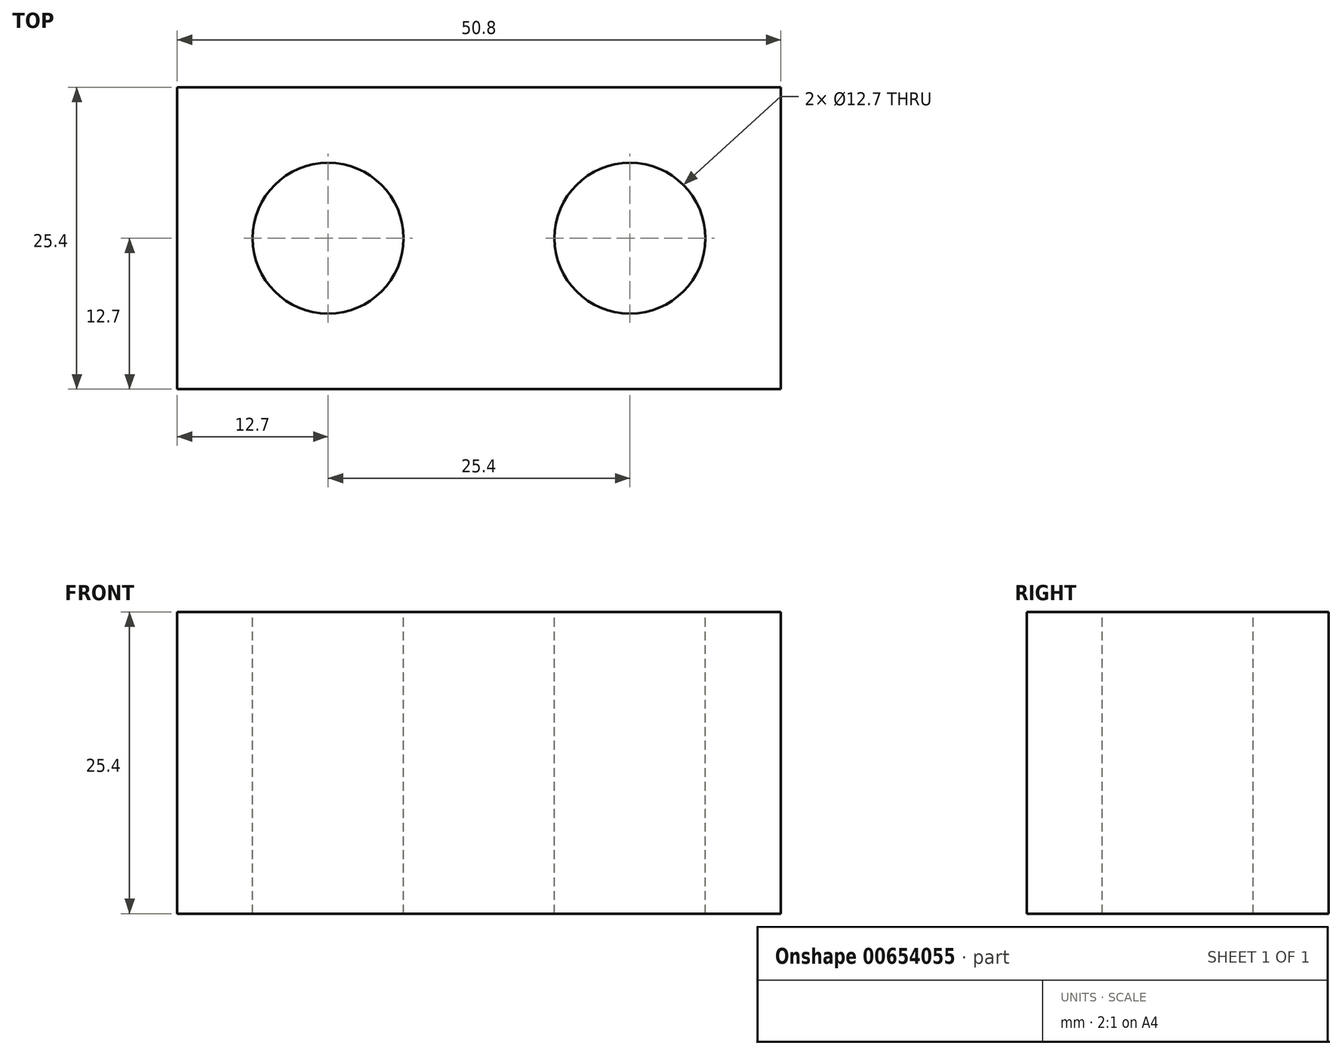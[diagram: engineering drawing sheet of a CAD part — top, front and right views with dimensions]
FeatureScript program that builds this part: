
annotation { "Feature Type Name" : "Feature", "Feature Type Description" : "" }
export const myFeature = defineFeature(function(context is Context, id is Id, definition is map)
    precondition{}
    {
        {
            var Q0;
            Q0=qCreatedBy(makeId("Top.planeOp"),FACE);
            var sketch = newSketch(context, id + "F0", { "sketchPlane" : qUnion([Q0])});
            skLineSegment(sketch, "E0.bottom", {"start": v(0, 0) * mm, "end": v(-50.8, 0) * mm});
            skLineSegment(sketch, "E0.top", {"start": v(0, 25.4) * mm, "end": v(-50.8, 25.4) * mm});
            skLineSegment(sketch, "E0.left", {"start": v(0, 0) * mm, "end": v(0, 25.4) * mm});
            skLineSegment(sketch, "E0.right", {"start": v(-50.8, 0) * mm, "end": v(-50.8, 25.4) * mm});
            skLineSegment(sketch, "E1", {"start": v(-25.4, 25.4) * mm, "end": v(-25.4, 0) * mm, "construction": true});
            skLineSegment(sketch, "E2", {"start": v(-25.4, 0) * mm, "end": v(-50.8, 25.4) * mm, "construction": true});
            skLineSegment(sketch, "E3", {"start": v(0, 25.4) * mm, "end": v(-25.4, 0) * mm, "construction": true});
            skCircle(sketch, "E4", {"center": v(-38.1, 12.7) * mm, "radius": 6.35 * mm});
            skCircle(sketch, "E5", {"center": v(-12.7, 12.7) * mm, "radius": 6.35 * mm});
            skSolve(sketch);
        }
        {
            var Q0;
            Q0=makeQuery(id+"F0.imprint","IMPRINT",FACE,{"disambiguationData":[TD([[makeQuery(id+"F0.imprint","IMPRINT",EDGE,{"derivedFrom":sQuery(id+"F0.wireOp",EDGE,"E0.bottom")}),-1.0]])]});
            extrude(context, id + "F1", {"entities" : qUnion([Q0]), "oppositeDirection" : true, "depth" : 25.4 * mm, "offsetDistance" : 25.4 * mm});
        }
    });
